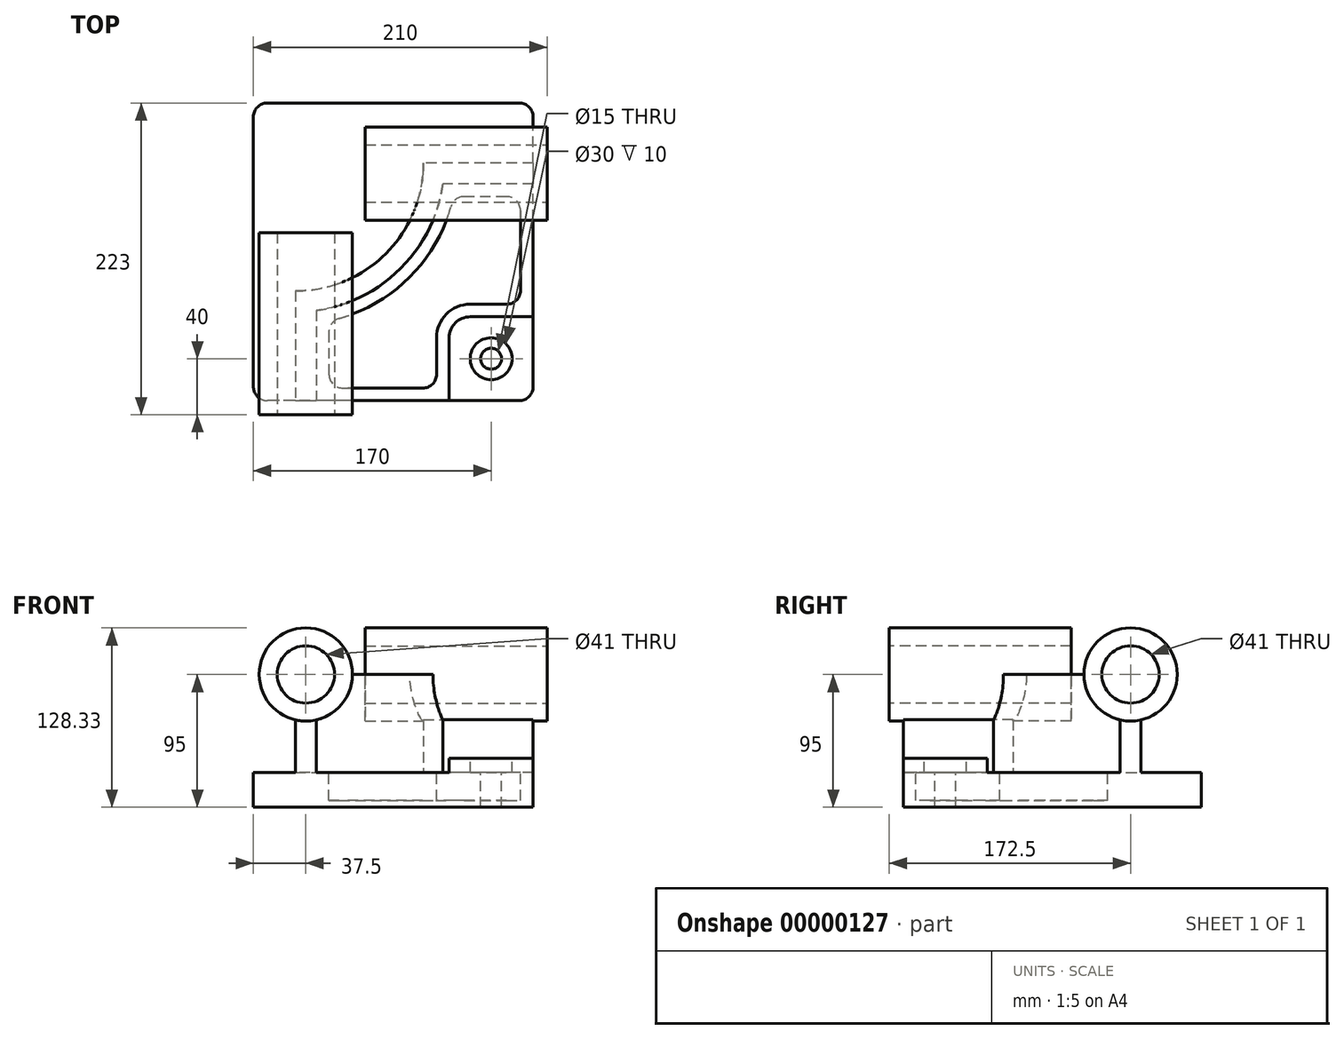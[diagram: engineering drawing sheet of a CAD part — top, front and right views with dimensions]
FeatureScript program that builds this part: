
annotation { "Feature Type Name" : "Feature", "Feature Type Description" : "" }
export const myFeature = defineFeature(function(context is Context, id is Id, definition is map)
    precondition{}
    {
        {
            assignVariable(context, id + "F0", {"name" : "D", "anyValue" : 130});
        }
        {
            var Q0;
            Q0=qCreatedBy(makeId("Top.planeOp"),FACE);
            var sketch = newSketch(context, id + "F1", { "sketchPlane" : qUnion([Q0])});
            skLineSegment(sketch, "E0.bottom", {"start": v(100, -106.5) * mm, "end": v(-100, -106.5) * mm});
            skLineSegment(sketch, "E0.top", {"start": v(100, 106.5) * mm, "end": v(-100, 106.5) * mm});
            skLineSegment(sketch, "E0.left", {"start": v(100, -106.5) * mm, "end": v(100, 106.5) * mm});
            skLineSegment(sketch, "E0.right", {"start": v(-100, -106.5) * mm, "end": v(-100, 106.5) * mm});
            skPoint(sketch, "E0.middle", {"position": v(0, 0) * mm});
            skSolve(sketch);
        }
        {
            var Q0;
            Q0=makeQuery(id+"F1.imprint","IMPRINT",FACE,{"disambiguationData":[TD([[makeQuery(id+"F1.imprint","IMPRINT",EDGE,{"derivedFrom":sQuery(id+"F1.wireOp",EDGE,"E0.bottom")}),-1.0]])]});
            extrude(context, id + "F2", {"entities" : qUnion([Q0]), "depth" : 25 * mm});
        }
        {
            var Q0;
            Q0=makeQuery(id+"F2.opExtrude","CAP_FACE",FACE,{"disambiguationData":[OSD([sQuery(id+"F1.wireOp",EDGE,"E0.bottom"),sQuery(id+"F1.wireOp",EDGE,"E0.top"),sQuery(id+"F1.wireOp",EDGE,"E0.left"),sQuery(id+"F1.wireOp",EDGE,"E0.right")])],"isStart":false});
            var sketch = newSketch(context, id + "F3", { "sketchPlane" : qUnion([Q0])});
            skLineSegment(sketch, "E1.bottom", {"start": v(100, -106.5) * mm, "end": v(40, -106.5) * mm});
            skLineSegment(sketch, "E1.top", {"start": v(100, -46.5) * mm, "end": v(40, -46.5) * mm});
            skLineSegment(sketch, "E1.left", {"start": v(100, -106.5) * mm, "end": v(100, -46.5) * mm});
            skLineSegment(sketch, "E1.right", {"start": v(40, -106.5) * mm, "end": v(40, -46.5) * mm});
            skSolve(sketch);
        }
        {
            var Q0;
            Q0=makeQuery(id+"F3.imprint","IMPRINT",FACE,{"disambiguationData":[TD([[makeQuery(id+"F3.imprint","IMPRINT",EDGE,{"derivedFrom":sQuery(id+"F3.wireOp",EDGE,"E1.bottom")}),-1.0]])]});
            extrude(context, id + "F4", {"entities" : qUnion([Q0]), "operationType" : NewBodyOperationType.ADD, "depth" : (35 - 25) * mm});
        }
        {
            var Q0;
            Q0=makeQuery(id+"F2.opExtrude","SWEPT_EDGE",EDGE,{"disambiguationData":[OSD([sQuery(id+"F1.wireOp",EDGE,"E0.bottom"),sQuery(id+"F1.wireOp",EDGE,"E0.right")])]});
            var Q1;
            Q1=makeQuery(id+"F2.opExtrude","SWEPT_EDGE",EDGE,{"disambiguationData":[OSD([sQuery(id+"F1.wireOp",EDGE,"E0.bottom"),sQuery(id+"F1.wireOp",EDGE,"E0.left")])]});
            var Q2;
            Q2=makeQuery(id+"F2.opExtrude","SWEPT_EDGE",EDGE,{"disambiguationData":[OSD([sQuery(id+"F1.wireOp",EDGE,"E0.top"),sQuery(id+"F1.wireOp",EDGE,"E0.left")])]});
            var Q3;
            Q3=makeQuery(id+"F2.opExtrude","SWEPT_EDGE",EDGE,{"disambiguationData":[OSD([sQuery(id+"F1.wireOp",EDGE,"E0.top"),sQuery(id+"F1.wireOp",EDGE,"E0.right")])]});
            fillet(context, id + "F5", {"entities" : qUnion([Q0, Q1, Q2, Q3]), "radius" : 10 * mm, "tangentPropagation" : true, "allowEdgeOverflow" : false});
        }
        {
            var Q0;
            Q0=makeQuery(id+"F2.opExtrude","CAP_FACE",FACE,{"disambiguationData":[OSD([sQuery(id+"F1.wireOp",EDGE,"E0.bottom"),sQuery(id+"F1.wireOp",EDGE,"E0.top"),sQuery(id+"F1.wireOp",EDGE,"E0.left"),sQuery(id+"F1.wireOp",EDGE,"E0.right")])],"isStart":false});
            var sketch = newSketch(context, id + "F6", { "sketchPlane" : qUnion([Q0])});
            skLineSegment(sketch, "E2", {"start": v(100, 63.5) * mm, "end": v(21.55, 63.5) * mm});
            skArc(sketch, "E3", {"start": v(21.55, 63.5) * mm, "mid": v(-5.26, -1.24) * mm, "end": v(-70, -28.05) * mm});
            skLineSegment(sketch, "E4", {"start": v(-70, -28.05) * mm, "end": v(-70, -106.5) * mm});
            skLineSegment(sketch, "E5.0", {"start": v(-55, -42) * mm, "end": v(-55, -106.5) * mm});
            skArc(sketch, "E5.1", {"start": v(35.5, 48.5) * mm, "mid": v(5.34, -11.84) * mm, "end": v(-55, -42) * mm});
            skLineSegment(sketch, "E5.2", {"start": v(100, 48.5) * mm, "end": v(35.5, 48.5) * mm});
            skSolve(sketch);
        }
        {
            var Q0;
            {var subQ3=sQuery(id+"F6.wireOp",EDGE,"E2");Q0=makeQuery(id+"F6.imprint","IMPRINT",FACE,{"disambiguationData":[TD([[makeQuery(id+"F6.imprint","IMPRINT",EDGE,{"derivedFrom":subQ3}),1.0]])]});}
            extrude(context, id + "F7", {"entities" : qUnion([Q0]), "operationType" : NewBodyOperationType.ADD, "depth" : (95 - 25) * mm});
        }
        {
            var Q0;
            Q0=makeQuery(id+"F4.opExtrude","SWEPT_EDGE",EDGE,{"disambiguationData":[OSD([sQuery(id+"F3.wireOp",EDGE,"E1.top"),sQuery(id+"F3.wireOp",EDGE,"E1.right")])]});
            fillet(context, id + "F8", {"entities" : qUnion([Q0]), "radius" : 15 * mm, "tangentPropagation" : true, "allowEdgeOverflow" : false});
        }
        {
            var Q0;
            {var subQ0=sQuery(id+"F1.wireOp",EDGE,"E0.bottom");var subQ1=sQuery(id+"F1.wireOp",EDGE,"E0.left");Q0=makeQuery(id+"F7.boolean.opBoolean","SPLIT",FACE,{"disambiguationData":[TD([makeQuery(id+"F4.opExtrude","SWEPT_FACE",FACE,{"disambiguationData":[OSD([sQuery(id+"F3.wireOp",EDGE,"E1.top")])]})])],"derivedFrom":makeQuery(id+"F2.opExtrude","CAP_FACE",FACE,{"disambiguationData":[OSD([subQ0,sQuery(id+"F1.wireOp",EDGE,"E0.top"),subQ1,sQuery(id+"F1.wireOp",EDGE,"E0.right")])],"isStart":false})});}
            var sketch = newSketch(context, id + "F9", { "sketchPlane" : qUnion([Q0])});
            skLineSegment(sketch, "E6.0", {"start": v(55, -37.5) * mm, "end": v(91, -37.5) * mm});
            skArc(sketch, "E6.1", {"start": v(31, -61.5) * mm, "mid": v(38.03, -44.53) * mm, "end": v(55, -37.5) * mm});
            skLineSegment(sketch, "E6.2", {"start": v(91, -37.5) * mm, "end": v(91, 39.5) * mm});
            skLineSegment(sketch, "E6.3", {"start": v(31, -97.5) * mm, "end": v(31, -61.5) * mm});
            skLineSegment(sketch, "E6.4", {"start": v(91, 39.5) * mm, "end": v(43.03, 39.5) * mm});
            skArc(sketch, "E6.5", {"start": v(43.03, 39.5) * mm, "mid": v(11.7, -18.2) * mm, "end": v(-46, -49.53) * mm});
            skLineSegment(sketch, "E6.6", {"start": v(-46, -49.53) * mm, "end": v(-46, -97.5) * mm});
            skLineSegment(sketch, "E6.7", {"start": v(-46, -97.5) * mm, "end": v(31, -97.5) * mm});
            skLineSegment(sketch, "E7.0", {"start": v(55, -51.5) * mm, "end": v(105, -51.5) * mm});
            skArc(sketch, "E7.1", {"start": v(45, -61.5) * mm, "mid": v(47.93, -54.43) * mm, "end": v(55, -51.5) * mm});
            skLineSegment(sketch, "E7.2", {"start": v(105, -51.5) * mm, "end": v(105, 53.5) * mm});
            skLineSegment(sketch, "E7.3", {"start": v(45, -111.5) * mm, "end": v(45, -61.5) * mm});
            skLineSegment(sketch, "E7.4", {"start": v(105, 53.5) * mm, "end": v(31.06, 53.5) * mm});
            skArc(sketch, "E7.5", {"start": v(31.06, 53.5) * mm, "mid": v(1.8, -8.3) * mm, "end": v(-60, -37.56) * mm});
            skLineSegment(sketch, "E7.6", {"start": v(-60, -37.56) * mm, "end": v(-60, -111.5) * mm});
            skLineSegment(sketch, "E7.7", {"start": v(-60, -111.5) * mm, "end": v(45, -111.5) * mm});
            skSolve(sketch);
        }
        {
            var Q0;
            Q0=qCreatedBy(makeId("Top.planeOp"),FACE);
            cPlane(context, id + "F10", {"entities" : qUnion([Q0]), "cplaneType" : CPlaneType.OFFSET, "offset" : 5 * mm, "width" : 150 * mm, "height" : 150 * mm});
        }
        {
            var Q0;
            Q0=makeQuery(id+"F9.imprint","IMPRINT",FACE,{"disambiguationData":[TD([[makeQuery(id+"F9.imprint","IMPRINT",EDGE,{"derivedFrom":sQuery(id+"F9.wireOp",EDGE,"E6.0")}),1.0]])]});
            var Q1;
            Q1=qCreatedBy(id+"F10.planeOp",FACE);
            extrude(context, id + "F11", {"entities" : qUnion([Q0]), "operationType" : NewBodyOperationType.REMOVE, "endBound" : BoundingType.UP_TO_SURFACE, "oppositeDirection" : true, "endBoundEntityFace" : qUnion([Q1]), "depth" : 25 * mm});
        }
        {
            var Q0;
            Q0=makeQuery(id+"F11.boolean.opBoolean","COPY",EDGE,{"derivedFrom":makeQuery(id+"F11.opExtrude","SWEPT_EDGE",EDGE,{"disambiguationData":[OSD([sQuery(id+"F9.wireOp",EDGE,"E6.5"),sQuery(id+"F9.wireOp",EDGE,"E6.6")])]})});
            var Q1;
            Q1=makeQuery(id+"F11.boolean.opBoolean","COPY",EDGE,{"derivedFrom":makeQuery(id+"F11.opExtrude","SWEPT_EDGE",EDGE,{"disambiguationData":[OSD([sQuery(id+"F9.wireOp",EDGE,"E6.4"),sQuery(id+"F9.wireOp",EDGE,"E6.5")])]})});
            var Q2;
            Q2=makeQuery(id+"F11.boolean.opBoolean","COPY",EDGE,{"derivedFrom":makeQuery(id+"F11.opExtrude","SWEPT_EDGE",EDGE,{"disambiguationData":[OSD([sQuery(id+"F9.wireOp",EDGE,"E6.3"),sQuery(id+"F9.wireOp",EDGE,"E6.7")])]})});
            var Q3;
            Q3=makeQuery(id+"F11.boolean.opBoolean","COPY",EDGE,{"derivedFrom":makeQuery(id+"F11.opExtrude","SWEPT_EDGE",EDGE,{"disambiguationData":[OSD([sQuery(id+"F9.wireOp",EDGE,"E6.0"),sQuery(id+"F9.wireOp",EDGE,"E6.2")])]})});
            var Q4;
            Q4=makeQuery(id+"F11.boolean.opBoolean","COPY",EDGE,{"derivedFrom":makeQuery(id+"F11.opExtrude","SWEPT_EDGE",EDGE,{"disambiguationData":[OSD([sQuery(id+"F9.wireOp",EDGE,"E6.2"),sQuery(id+"F9.wireOp",EDGE,"E6.4")])]})});
            var Q5;
            Q5=makeQuery(id+"F11.boolean.opBoolean","COPY",EDGE,{"derivedFrom":makeQuery(id+"F11.opExtrude","SWEPT_EDGE",EDGE,{"disambiguationData":[OSD([sQuery(id+"F9.wireOp",EDGE,"E6.6"),sQuery(id+"F9.wireOp",EDGE,"E6.7")])]})});
            fillet(context, id + "F12", {"entities" : qUnion([Q0, Q1, Q2, Q3, Q4, Q5]), "radius" : 10 * mm, "tangentPropagation" : true, "allowEdgeOverflow" : false});
        }
        {
            var Q0;
            {var subQ0=sQuery(id+"F1.wireOp",EDGE,"E0.left");Q0=makeQuery(id+"F7.boolean.opBoolean","MERGE",FACE,{"derivedFrom":[makeQuery(id+"F4.boolean.opBoolean","MERGE",FACE,{"derivedFrom":[makeQuery(id+"F2.opExtrude","SWEPT_FACE",FACE,{"disambiguationData":[OSD([subQ0])]}),makeQuery(id+"F4.opExtrude","SWEPT_FACE",FACE,{"disambiguationData":[OSD([sQuery(id+"F3.wireOp",EDGE,"E1.left")])]})]}),makeQuery(id+"F7.opExtrude","SWEPT_FACE",FACE,{"disambiguationData":[OSD([subQ0])]})]});}
            cPlane(context, id + "F13", {"entities" : qUnion([Q0]), "cplaneType" : CPlaneType.OFFSET, "offset" : 10 * mm, "width" : 150 * mm, "height" : 150 * mm});
        }
        {
            var Q0;
            {var subQ0=sQuery(id+"F1.wireOp",EDGE,"E0.bottom");Q0=makeQuery(id+"F7.boolean.opBoolean","MERGE",FACE,{"derivedFrom":[makeQuery(id+"F4.boolean.opBoolean","MERGE",FACE,{"derivedFrom":[makeQuery(id+"F2.opExtrude","SWEPT_FACE",FACE,{"disambiguationData":[OSD([subQ0])]}),makeQuery(id+"F4.opExtrude","SWEPT_FACE",FACE,{"disambiguationData":[OSD([sQuery(id+"F3.wireOp",EDGE,"E1.bottom")])]})]}),makeQuery(id+"F7.opExtrude","SWEPT_FACE",FACE,{"disambiguationData":[OSD([subQ0])]})]});}
            cPlane(context, id + "F14", {"entities" : qUnion([Q0]), "cplaneType" : CPlaneType.OFFSET, "offset" : 10 * mm, "width" : 150 * mm, "height" : 150 * mm});
        }
        {
            var Q0;
            Q0=qCreatedBy(id+"F13.planeOp",FACE);
            var sketch = newSketch(context, id + "F15", { "sketchPlane" : qUnion([Q0])});
            skCircle(sketch, "E8", {"center": v(56, 95) * mm, "radius": 33.33 * mm});
            skCircle(sketch, "E9", {"center": v(56, 95) * mm, "radius": 20.5 * mm});
            skSolve(sketch);
        }
        {
            var Q0;
            Q0 = qSketchRegion(id + "F15", true);
            var Q1;
            Q1=makeQuery(id+"F15.imprint","IMPRINT",FACE,{"disambiguationData":[TD([[makeQuery(id+"F15.imprint","IMPRINT",EDGE,{"derivedFrom":sQuery(id+"F15.wireOp",EDGE,"E9")}),1.0]])]});
            extrude(context, id + "F16", {"entities" : qUnion([Q0, Q1]), "operationType" : NewBodyOperationType.ADD, "oppositeDirection" : true, "depth" : (getVariable(context, 'D')) * mm});
        }
        {
            var Q0;
            Q0=makeQuery(id+"F15.imprint","IMPRINT",FACE,{"disambiguationData":[TD([[makeQuery(id+"F15.imprint","IMPRINT",EDGE,{"derivedFrom":sQuery(id+"F15.wireOp",EDGE,"E9")}),1.0]])]});
            extrude(context, id + "F17", {"entities" : qUnion([Q0]), "operationType" : NewBodyOperationType.REMOVE, "endBound" : BoundingType.THROUGH_ALL, "oppositeDirection" : true, "depth" : 25 * mm});
        }
        {
            var Q0;
            Q0=qCreatedBy(id+"F14.planeOp",FACE);
            var sketch = newSketch(context, id + "F18", { "sketchPlane" : qUnion([Q0])});
            skCircle(sketch, "E10", {"center": v(-62.5, 95) * mm, "radius": 33.33 * mm});
            skCircle(sketch, "E11", {"center": v(-62.5, 95) * mm, "radius": 20.5 * mm});
            skSolve(sketch);
        }
        {
            var Q0;
            Q0=makeQuery(id+"F18.imprint","IMPRINT",FACE,{"disambiguationData":[TD([[makeQuery(id+"F18.imprint","IMPRINT",EDGE,{"derivedFrom":sQuery(id+"F18.wireOp",EDGE,"E10")}),1.0]])]});
            var Q1;
            Q1=makeQuery(id+"F18.imprint","IMPRINT",FACE,{"disambiguationData":[TD([[makeQuery(id+"F18.imprint","IMPRINT",EDGE,{"derivedFrom":sQuery(id+"F18.wireOp",EDGE,"E11")}),1.0]])]});
            extrude(context, id + "F19", {"entities" : qUnion([Q0, Q1]), "operationType" : NewBodyOperationType.ADD, "oppositeDirection" : true, "depth" : (getVariable(context, 'D')) * mm});
        }
        {
            var Q0;
            Q0=makeQuery(id+"F18.imprint","IMPRINT",FACE,{"disambiguationData":[TD([[makeQuery(id+"F18.imprint","IMPRINT",EDGE,{"derivedFrom":sQuery(id+"F18.wireOp",EDGE,"E11")}),1.0]])]});
            extrude(context, id + "F20", {"entities" : qUnion([Q0]), "operationType" : NewBodyOperationType.REMOVE, "endBound" : BoundingType.THROUGH_ALL, "oppositeDirection" : true, "depth" : 25 * mm});
        }
        {
            var Q0;
            Q0=makeQuery(id+"F4.opExtrude","CAP_FACE",FACE,{"disambiguationData":[OSD([sQuery(id+"F3.wireOp",EDGE,"E1.bottom"),sQuery(id+"F3.wireOp",EDGE,"E1.top"),sQuery(id+"F3.wireOp",EDGE,"E1.left"),sQuery(id+"F3.wireOp",EDGE,"E1.right")])],"isStart":false});
            var sketch = newSketch(context, id + "F21", { "sketchPlane" : qUnion([Q0])});
            skPoint(sketch, "E12", {"position": v(70, -76.5) * mm});
            skSolve(sketch);
        }
        {
            var Q0;
            Q0=sQuery(id+"F21.wireOp",VERTEX,"E12");
            var Q1;
            Q1=makeQuery(id+"F2.opExtrude","SWEPT_BODY",BODY,{"disambiguationData":[OSD([sQuery(id+"F1.wireOp",EDGE,"E0.bottom"),sQuery(id+"F1.wireOp",EDGE,"E0.top"),sQuery(id+"F1.wireOp",EDGE,"E0.left"),sQuery(id+"F1.wireOp",EDGE,"E0.right")])]});
            hole(context, id + "F22", {"style" : HoleStyle.C_BORE, "endStyle" : HoleEndStyle.THROUGH, "holeDiameter" : 15 * mm, "cBoreDiameter" : 30 * mm, "cBoreDepth" : 10 * mm, "isTappedThrough" : true, "tappedDepth" : 12 * mm, "tapClearance" : 3, "locations" : qUnion([Q0]), "scope" : qUnion([Q1])});
        }
    });
